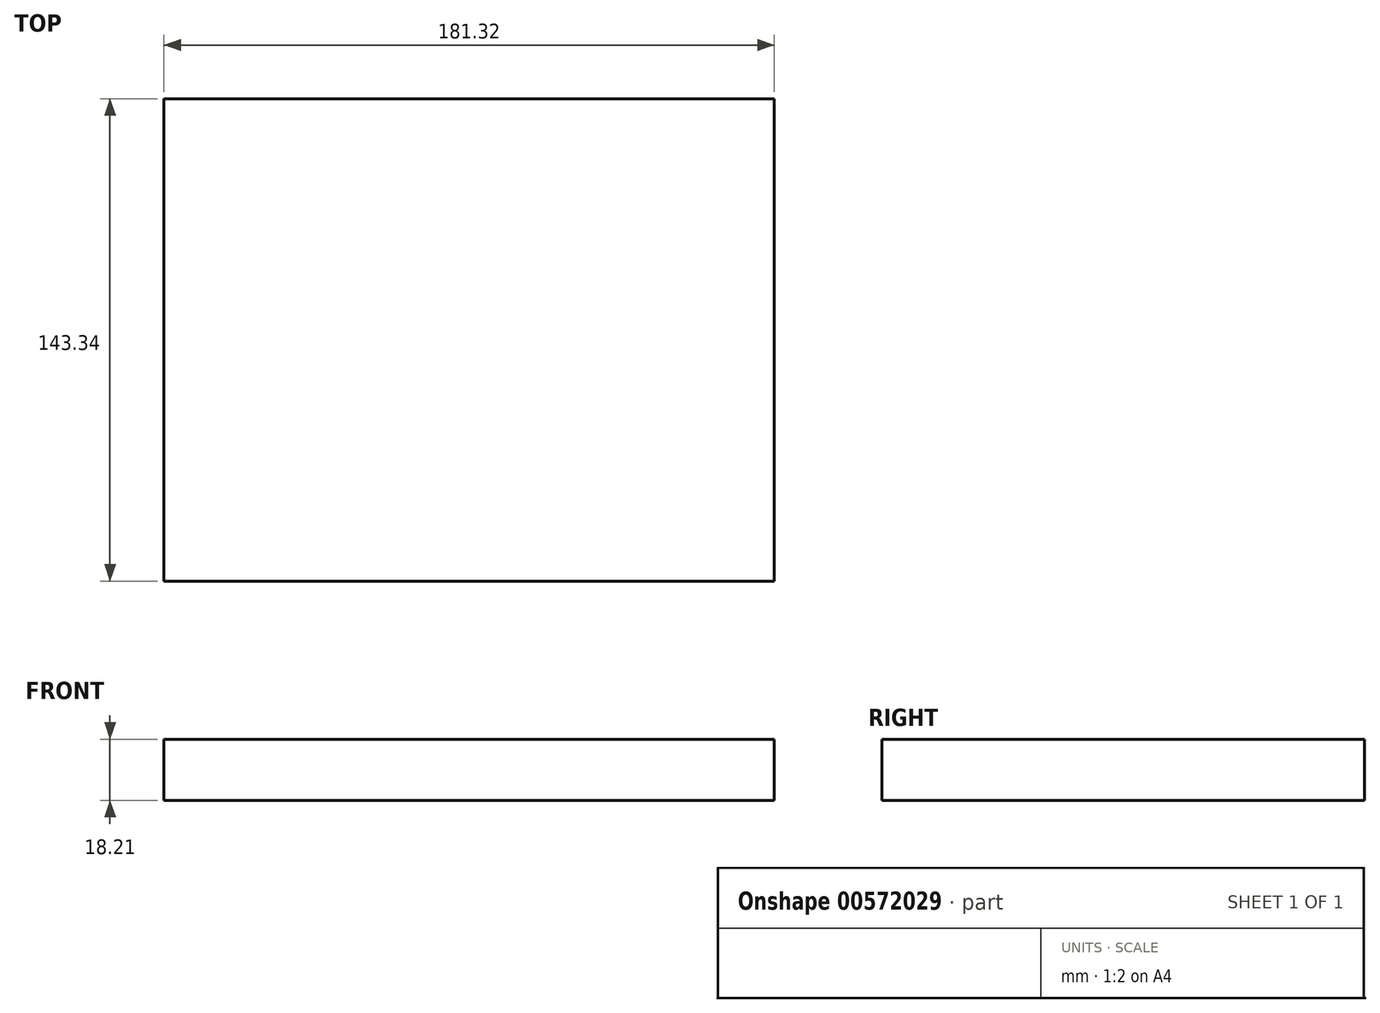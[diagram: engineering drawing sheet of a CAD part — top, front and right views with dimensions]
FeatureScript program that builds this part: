
annotation { "Feature Type Name" : "Feature", "Feature Type Description" : "" }
export const myFeature = defineFeature(function(context is Context, id is Id, definition is map)
    precondition{}
    {
        {
            var Q0;
            Q0=qCreatedBy(makeId("Right.planeOp"),FACE);
            var sketch = newSketch(context, id + "F0", { "sketchPlane" : qUnion([Q0])});
            skLineSegment(sketch, "E0.bottom", {"start": v(0, 0) * mm, "end": v(143.34, 0) * mm});
            skLineSegment(sketch, "E0.top", {"start": v(0, -18.2) * mm, "end": v(143.34, -18.2) * mm});
            skLineSegment(sketch, "E0.left", {"start": v(0, 0) * mm, "end": v(0, -18.2) * mm});
            skLineSegment(sketch, "E0.right", {"start": v(143.34, 0) * mm, "end": v(143.34, -18.2) * mm});
            skSolve(sketch);
        }
        {
            var Q0;
            Q0=makeQuery(id+"F0.imprint","IMPRINT",FACE,{"disambiguationData":[TD([[makeQuery(id+"F0.imprint","IMPRINT",EDGE,{"derivedFrom":sQuery(id+"F0.wireOp",EDGE,"E0.bottom")}),-1.0]])]});
            extrude(context, id + "F1", {"entities" : qUnion([Q0]), "oppositeDirection" : true, "depth" : 181.32 * mm, "offsetDistance" : 25.4 * mm});
        }
    });
